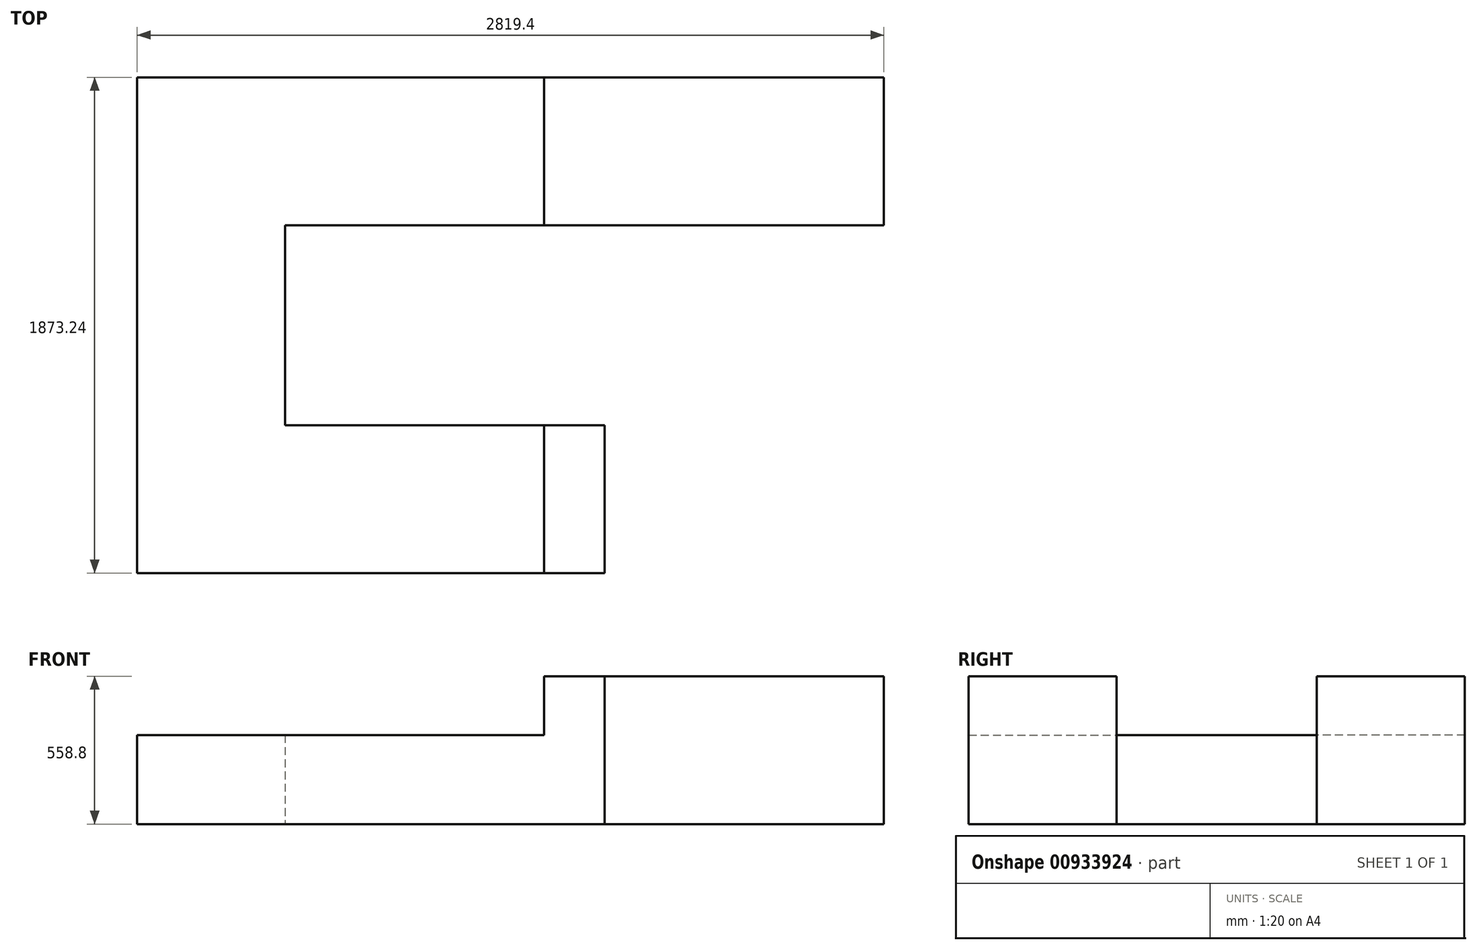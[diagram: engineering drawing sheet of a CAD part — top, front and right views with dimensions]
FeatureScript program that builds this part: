
annotation { "Feature Type Name" : "Feature", "Feature Type Description" : "" }
export const myFeature = defineFeature(function(context is Context, id is Id, definition is map)
    precondition{}
    {
        {
            var Q0;
            Q0=qCreatedBy(makeId("Top.planeOp"),FACE);
            var sketch = newSketch(context, id + "F0", { "sketchPlane" : qUnion([Q0])});
            skLineSegment(sketch, "E0.bottom", {"start": v(-1409.7, 936.62) * mm, "end": v(1409.7, 936.62) * mm});
            skLineSegment(sketch, "E0.top", {"start": v(-1409.7, -936.62) * mm, "end": v(1409.7, -936.62) * mm});
            skLineSegment(sketch, "E0.left", {"start": v(-1409.7, 936.62) * mm, "end": v(-1409.7, -936.62) * mm});
            skLineSegment(sketch, "E0.right", {"start": v(1409.7, 936.62) * mm, "end": v(1409.7, -936.62) * mm});
            skLineSegment(sketch, "E1.bottom", {"start": v(-1409.7, 936.62) * mm, "end": v(-850.9, 936.62) * mm});
            skLineSegment(sketch, "E1.top", {"start": v(-1409.7, -936.62) * mm, "end": v(-850.9, -936.62) * mm});
            skLineSegment(sketch, "E2.bottom", {"start": v(-850.9, 936.62) * mm, "end": v(127, 936.62) * mm});
            skLineSegment(sketch, "E2.top", {"start": v(-850.9, 377.83) * mm, "end": v(127, 377.83) * mm});
            skLineSegment(sketch, "E2.left", {"start": v(-850.9, 936.62) * mm, "end": v(-850.9, 377.83) * mm});
            skLineSegment(sketch, "E2.right", {"start": v(127, 936.63) * mm, "end": v(127, 377.83) * mm});
            skLineSegment(sketch, "E3.bottom", {"start": v(-850.9, -936.62) * mm, "end": v(127, -936.62) * mm});
            skLineSegment(sketch, "E3.top", {"start": v(-850.9, -377.82) * mm, "end": v(127, -377.82) * mm});
            skLineSegment(sketch, "E3.left", {"start": v(-850.9, -936.62) * mm, "end": v(-850.9, -377.82) * mm});
            skLineSegment(sketch, "E3.right", {"start": v(127, -936.62) * mm, "end": v(127, -377.82) * mm});
            skLineSegment(sketch, "E4.bottom", {"start": v(127, 936.62) * mm, "end": v(1409.7, 936.62) * mm});
            skLineSegment(sketch, "E4.top", {"start": v(127, 377.83) * mm, "end": v(1409.7, 377.83) * mm});
            skLineSegment(sketch, "E4.left", {"start": v(127, 936.62) * mm, "end": v(127, 377.83) * mm});
            skLineSegment(sketch, "E4.right", {"start": v(1409.7, 936.62) * mm, "end": v(1409.7, 377.83) * mm});
            skLineSegment(sketch, "E5.bottom", {"start": v(127, -377.82) * mm, "end": v(355.6, -377.82) * mm});
            skLineSegment(sketch, "E5.top", {"start": v(127, -936.62) * mm, "end": v(355.6, -936.62) * mm});
            skLineSegment(sketch, "E5.left", {"start": v(127, -377.82) * mm, "end": v(127, -936.62) * mm});
            skLineSegment(sketch, "E5.right", {"start": v(355.6, -377.82) * mm, "end": v(355.6, -936.62) * mm});
            skLineSegment(sketch, "E6", {"start": v(-850.9, 377.83) * mm, "end": v(-850.9, -377.82) * mm});
            skSolve(sketch);
        }
        {
            var Q0;
            Q0=sQuery(id+"F0.wireOp",EDGE,"E2.top");
            var Q1;
            Q1=sQuery(id+"F0.wireOp",EDGE,"E3.top");
            var Q2;
            Q2=sQuery(id+"F0.wireOp",EDGE,"E3.right");
            var Q3;
            Q3=sQuery(id+"F0.wireOp",EDGE,"E3.left");
            var Q4;
            Q4=sQuery(id+"F0.wireOp",EDGE,"E2.left");
            extrude(context, id + "F1", {"bodyType" : ToolBodyType.SURFACE, "surfaceEntities" : qUnion([Q0, Q1, Q2, Q3, Q4]), "depth" : 336.55 * mm, "offsetDistance" : 25.4 * mm});
        }
        {
            var Q0;
            Q0=sQuery(id+"F0.wireOp",EDGE,"E6");
            extrude(context, id + "F2", {"bodyType" : ToolBodyType.SURFACE, "surfaceEntities" : qUnion([Q0]), "depth" : 336.55 * mm, "offsetDistance" : 25.4 * mm});
        }
        {
            var Q0;
            Q0=sQuery(id+"F0.wireOp",EDGE,"E4.top");
            var Q1;
            Q1=sQuery(id+"F0.wireOp",EDGE,"E2.right");
            var Q2;
            Q2=sQuery(id+"F0.wireOp",EDGE,"E5.bottom");
            var Q3;
            Q3=sQuery(id+"F0.wireOp",EDGE,"E5.right");
            extrude(context, id + "F3", {"bodyType" : ToolBodyType.SURFACE, "surfaceEntities" : qUnion([Q0, Q1, Q2, Q3]), "depth" : 558.8 * mm, "offsetDistance" : 25.4 * mm});
        }
        {
            var Q0;
            Q0=makeQuery(id+"F0.imprint","IMPRINT",FACE,{"disambiguationData":[TD([[makeQuery(id+"F0.imprint","IMPRINT",EDGE,{"derivedFrom":sQuery(id+"F0.wireOp",EDGE,"E3.top")}),-1.0]])]});
            var Q1;
            Q1=makeQuery(id+"F0.imprint","IMPRINT",FACE,{"disambiguationData":[TD([[makeQuery(id+"F0.imprint","IMPRINT",EDGE,{"derivedFrom":sQuery(id+"F0.wireOp",EDGE,"E2.top")}),1.0]])]});
            var Q2;
            {var subQ1=sQuery(id+"F0.wireOp",EDGE,"E0.left");Q2=makeQuery(id+"F0.imprint","IMPRINT",FACE,{"disambiguationData":[TD([[makeQuery(id+"F0.imprint","IMPRINT",EDGE,{"derivedFrom":subQ1}),1.0]])]});}
            extrude(context, id + "F4", {"entities" : qUnion([Q0, Q1, Q2]), "depth" : 336.55 * mm, "offsetDistance" : 25.4 * mm});
        }
        {
            var Q0;
            {var subQ2=sQuery(id+"F0.wireOp",EDGE,"E3.right");Q0=makeQuery(id+"F0.imprint","IMPRINT",FACE,{"disambiguationData":[TD([[makeQuery(id+"F0.imprint","IMPRINT",EDGE,{"derivedFrom":subQ2}),-1.0]])]});}
            var Q1;
            {var subQ0=sQuery(id+"F0.wireOp",EDGE,"E2.right");Q1=makeQuery(id+"F0.imprint","IMPRINT",FACE,{"disambiguationData":[TD([[makeQuery(id+"F0.imprint","IMPRINT",EDGE,{"derivedFrom":subQ0}),1.0]])]});}
            extrude(context, id + "F5", {"entities" : qUnion([Q0, Q1]), "operationType" : NewBodyOperationType.ADD, "depth" : 558.8 * mm, "offsetDistance" : 25.4 * mm});
        }
    });
